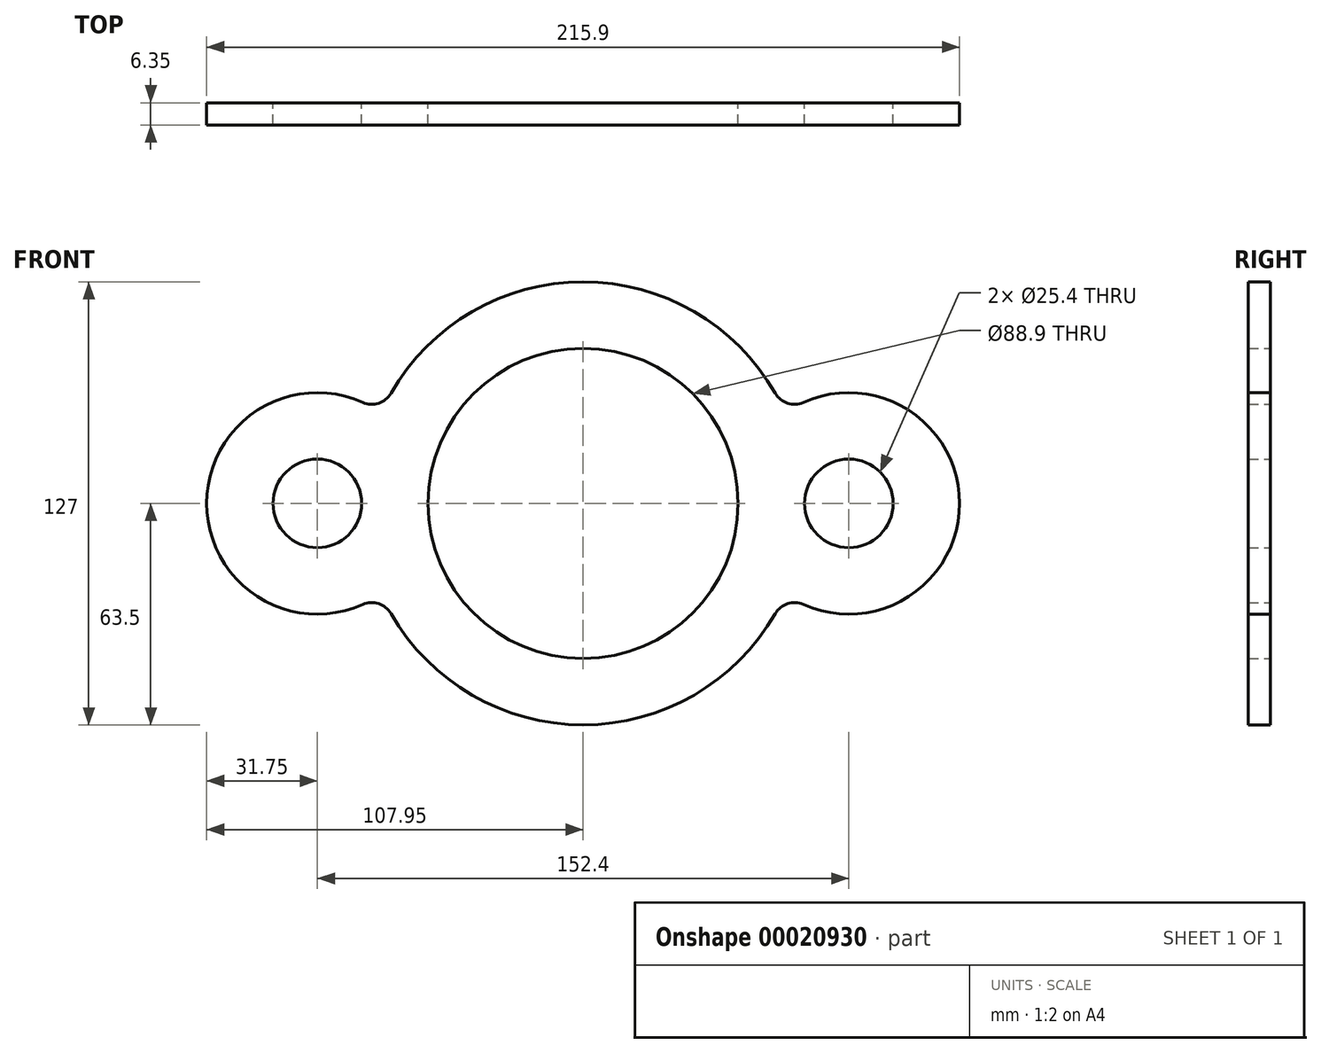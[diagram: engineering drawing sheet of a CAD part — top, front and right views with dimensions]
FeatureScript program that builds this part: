
annotation { "Feature Type Name" : "Feature", "Feature Type Description" : "" }
export const myFeature = defineFeature(function(context is Context, id is Id, definition is map)
    precondition{}
    {
        {
            var Q0;
            Q0=qCreatedBy(makeId("Front.planeOp"),FACE);
            var sketch = newSketch(context, id + "F0", { "sketchPlane" : qUnion([Q0])});
            skCircle(sketch, "E0", {"center": v(0, 0) * mm, "radius": 44.45 * mm});
            skArc(sketch, "E1", {"start": v(-63.2, 28.96) * mm, "mid": v(-107.95, 0) * mm, "end": v(-63.2, -28.96) * mm});
            skArc(sketch, "E2", {"start": v(63.2, -28.96) * mm, "mid": v(107.95, 0) * mm, "end": v(63.2, 28.96) * mm});
            skCircle(sketch, "E3", {"center": v(-76.2, 0) * mm, "radius": 12.7 * mm});
            skCircle(sketch, "E4", {"center": v(76.2, 0) * mm, "radius": 12.7 * mm});
            skArc(sketch, "E5", {"start": v(-55.08, -31.6) * mm, "mid": v(0, -63.5) * mm, "end": v(55.08, -31.6) * mm});
            skArc(sketch, "E6.trimOffspring", {"start": v(55.08, 31.6) * mm, "mid": v(0, 63.5) * mm, "end": v(-55.08, 31.6) * mm});
            skPoint(sketch, "E7.visualSharp", {"position": v(-57.94, 25.98) * mm});
            skArc(sketch, "E7.filletArc", {"start": v(-63.2, 28.96) * mm, "mid": v(-58.63, 28.72) * mm, "end": v(-55.08, 31.6) * mm});
            skPoint(sketch, "E8.visualSharp", {"position": v(-57.94, -25.98) * mm});
            skArc(sketch, "E8.filletArc", {"start": v(-55.08, -31.6) * mm, "mid": v(-58.63, -28.72) * mm, "end": v(-63.2, -28.96) * mm});
            skPoint(sketch, "E9.visualSharp", {"position": v(57.94, 25.98) * mm});
            skArc(sketch, "E9.filletArc", {"start": v(55.08, 31.6) * mm, "mid": v(58.63, 28.72) * mm, "end": v(63.2, 28.96) * mm});
            skPoint(sketch, "E10.visualSharp", {"position": v(57.94, -25.98) * mm});
            skArc(sketch, "E10.filletArc", {"start": v(63.2, -28.96) * mm, "mid": v(58.63, -28.72) * mm, "end": v(55.08, -31.6) * mm});
            skSolve(sketch);
        }
        {
            var Q0;
            Q0 = qSketchRegion(id + "F0", true);
            extrude(context, id + "F1", {"entities" : qUnion([Q0]), "depth" : 6.35 * mm});
        }
    });
